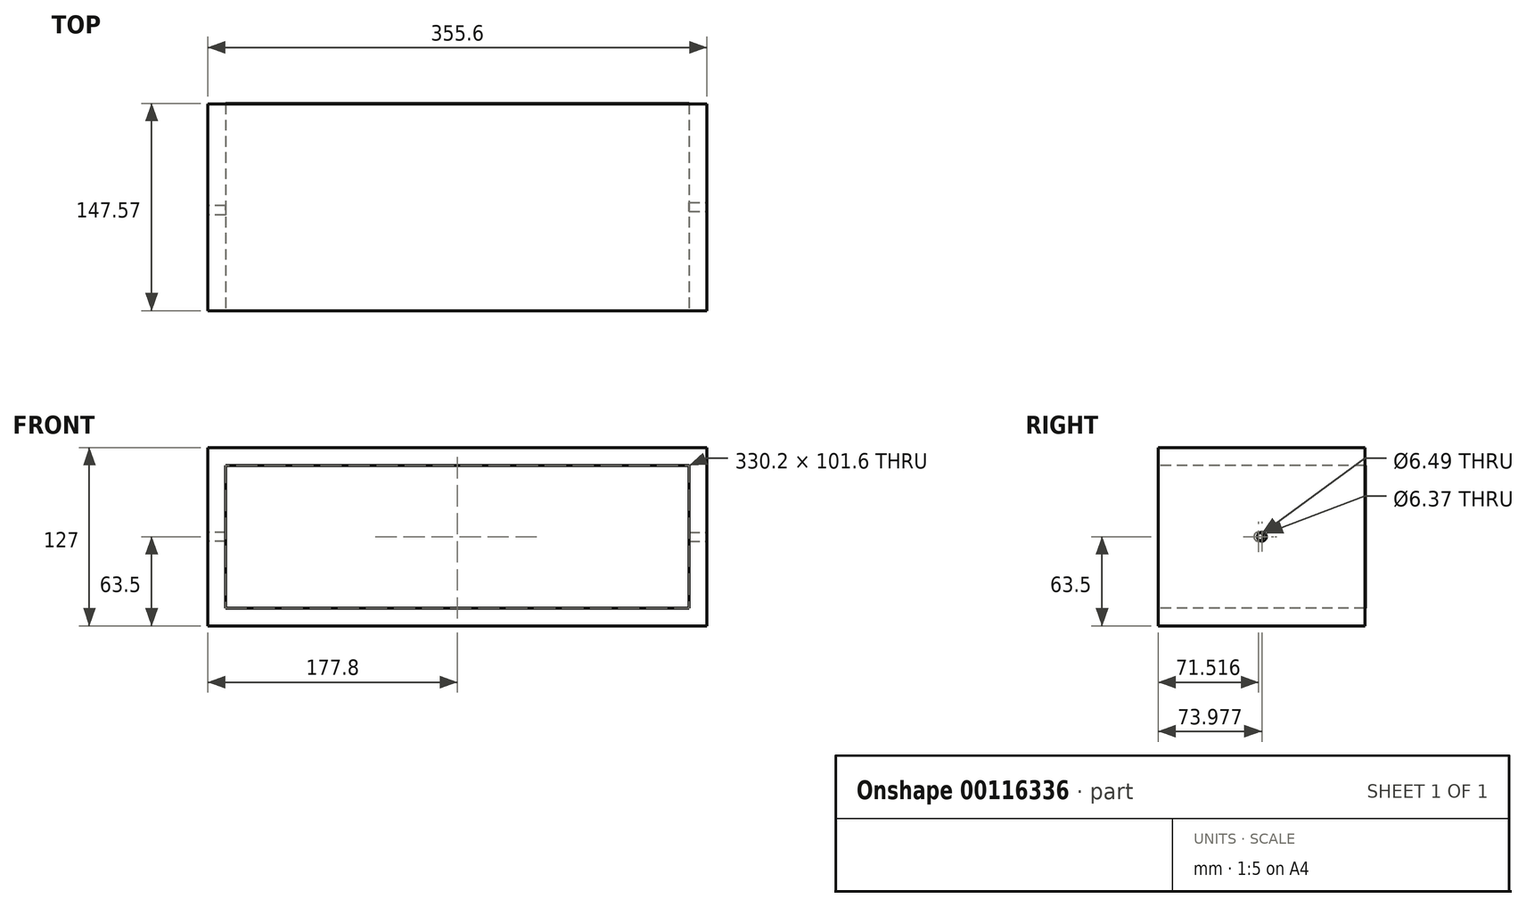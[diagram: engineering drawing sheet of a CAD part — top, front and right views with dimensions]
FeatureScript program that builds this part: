
annotation { "Feature Type Name" : "Feature", "Feature Type Description" : "" }
export const myFeature = defineFeature(function(context is Context, id is Id, definition is map)
    precondition{}
    {
        {
            var Q0;
            Q0=qCreatedBy(makeId("Front.planeOp"),FACE);
            var sketch = newSketch(context, id + "F0", { "sketchPlane" : qUnion([Q0])});
            skLineSegment(sketch, "E0.bottom", {"start": v(177.8, -63.5) * mm, "end": v(-177.8, -63.5) * mm});
            skLineSegment(sketch, "E0.top", {"start": v(177.8, 63.5) * mm, "end": v(-177.8, 63.5) * mm});
            skLineSegment(sketch, "E0.left", {"start": v(177.8, -63.5) * mm, "end": v(177.8, 63.5) * mm});
            skLineSegment(sketch, "E0.right", {"start": v(-177.8, -63.5) * mm, "end": v(-177.8, 63.5) * mm});
            skPoint(sketch, "E0.middle", {"position": v(0, 0) * mm});
            skSolve(sketch);
        }
        {
            var Q0;
            Q0 = qSketchRegion(id + "F0", true);
            extrude(context, id + "F1", {"entities" : qUnion([Q0]), "depth" : 147.32 * mm});
        }
        {
            var Q0;
            Q0=makeQuery(id+"F1.opExtrude","CAP_FACE",FACE,{"disambiguationData":[OSD([sQuery(id+"F0.wireOp",EDGE,"E0.bottom"),sQuery(id+"F0.wireOp",EDGE,"E0.top"),sQuery(id+"F0.wireOp",EDGE,"E0.left"),sQuery(id+"F0.wireOp",EDGE,"E0.right")])],"isStart":false});
            var sketch = newSketch(context, id + "F2", { "sketchPlane" : qUnion([Q0])});
            skLineSegment(sketch, "E1.bottom", {"start": v(165.1, -50.8) * mm, "end": v(-165.1, -50.8) * mm});
            skLineSegment(sketch, "E1.top", {"start": v(165.1, 50.8) * mm, "end": v(-165.1, 50.8) * mm});
            skLineSegment(sketch, "E1.left", {"start": v(165.1, -50.8) * mm, "end": v(165.1, 50.8) * mm});
            skLineSegment(sketch, "E1.right", {"start": v(-165.1, -50.8) * mm, "end": v(-165.1, 50.8) * mm});
            skPoint(sketch, "E1.middle", {"position": v(0, 0) * mm});
            skSolve(sketch);
        }
        {
            var Q0;
            Q0 = qSketchRegion(id + "F2", true);
            extrude(context, id + "F3", {"entities" : qUnion([Q0]), "operationType" : NewBodyOperationType.REMOVE, "endBound" : BoundingType.UP_TO_NEXT, "oppositeDirection" : true, "depth" : 25.4 * mm});
        }
        {
            var Q0;
            Q0=makeQuery(id+"F1.opExtrude","CAP_FACE",FACE,{"disambiguationData":[OSD([sQuery(id+"F0.wireOp",EDGE,"E0.bottom"),sQuery(id+"F0.wireOp",EDGE,"E0.top"),sQuery(id+"F0.wireOp",EDGE,"E0.left"),sQuery(id+"F0.wireOp",EDGE,"E0.right")])],"isStart":true});
            var sketch = newSketch(context, id + "F4", { "sketchPlane" : qUnion([Q0])});
            skLineSegment(sketch, "E2.bottom", {"start": v(-165.1, 50.8) * mm, "end": v(165.1, 50.8) * mm});
            skLineSegment(sketch, "E2.top", {"start": v(-165.1, -50.8) * mm, "end": v(165.1, -50.8) * mm});
            skLineSegment(sketch, "E2.left", {"start": v(-165.1, 50.8) * mm, "end": v(-165.1, -50.8) * mm});
            skLineSegment(sketch, "E2.right", {"start": v(165.1, 50.8) * mm, "end": v(165.1, -50.8) * mm});
            skSolve(sketch);
        }
        {
            var Q0;
            Q0=makeQuery(id+"F4.imprint","IMPRINT",FACE,{"disambiguationData":[TD([[makeQuery(id+"F4.imprint","IMPRINT",EDGE,{"derivedFrom":sQuery(id+"F4.wireOp",EDGE,"E2.bottom")}),1.0]])]});
            extrude(context, id + "F5", {"entities" : qUnion([Q0]), "depth" : 0.25 * mm});
        }
        {
            var Q0;
            Q0=makeQuery(id+"F1.opExtrude","SWEPT_FACE",FACE,{"disambiguationData":[OSD([sQuery(id+"F0.wireOp",EDGE,"E0.right")])]});
            var sketch = newSketch(context, id + "F6", { "sketchPlane" : qUnion([Q0])});
            skCircle(sketch, "E3", {"center": v(75.8, 0) * mm, "radius": 3.25 * mm});
            skSolve(sketch);
        }
        {
            var Q0;
            Q0 = qSketchRegion(id + "F6", true);
            extrude(context, id + "F7", {"entities" : qUnion([Q0]), "operationType" : NewBodyOperationType.REMOVE, "oppositeDirection" : true, "depth" : 25.4 * mm});
        }
        {
            var Q0;
            Q0=makeQuery(id+"F1.opExtrude","SWEPT_FACE",FACE,{"disambiguationData":[OSD([sQuery(id+"F0.wireOp",EDGE,"E0.left")])]});
            var sketch = newSketch(context, id + "F8", { "sketchPlane" : qUnion([Q0])});
            skCircle(sketch, "E4", {"center": v(-73.34, 0) * mm, "radius": 3.19 * mm});
            skSolve(sketch);
        }
        {
            var Q0;
            Q0 = qSketchRegion(id + "F8", true);
            extrude(context, id + "F9", {"entities" : qUnion([Q0]), "operationType" : NewBodyOperationType.REMOVE, "oppositeDirection" : true, "depth" : 25.4 * mm});
        }
    });
